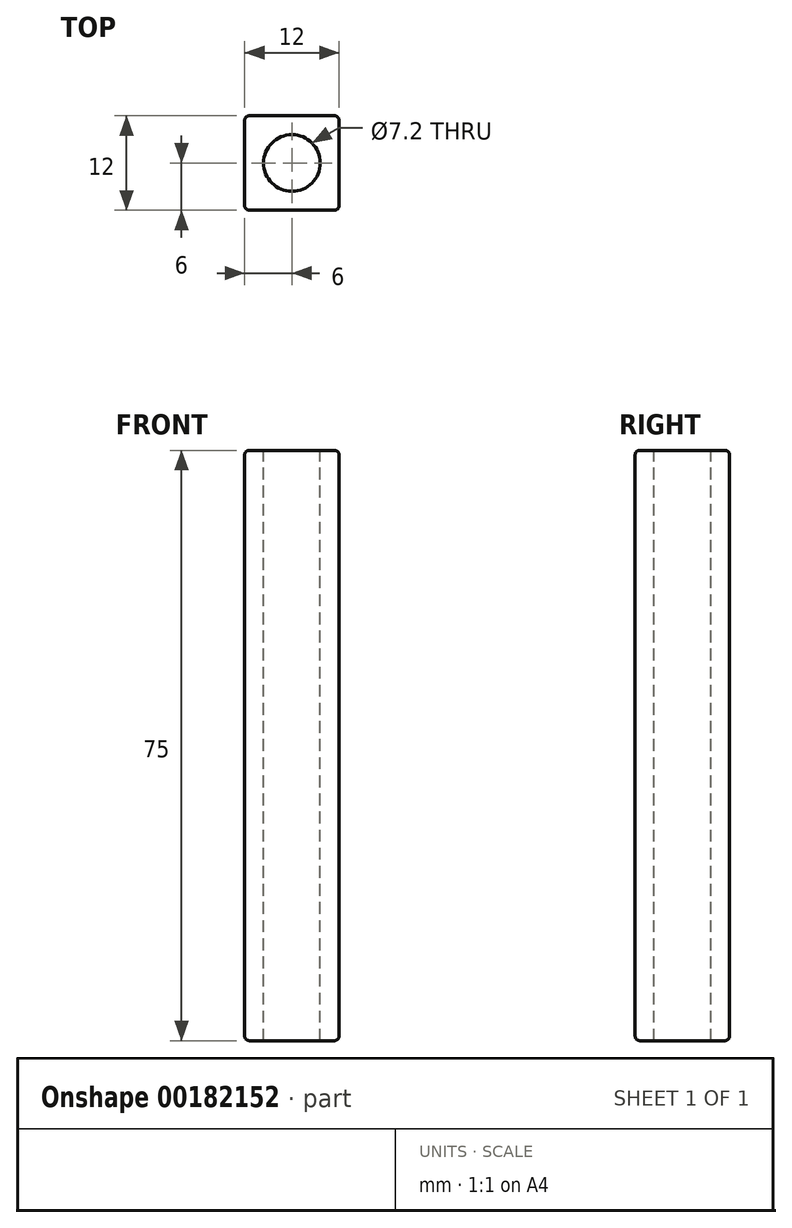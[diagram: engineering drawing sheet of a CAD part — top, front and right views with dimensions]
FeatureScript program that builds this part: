
annotation { "Feature Type Name" : "Feature", "Feature Type Description" : "" }
export const myFeature = defineFeature(function(context is Context, id is Id, definition is map)
    precondition{}
    {
        {
            var Q0;
            Q0=qCreatedBy(makeId("Top.planeOp"),FACE);
            var sketch = newSketch(context, id + "F0", { "sketchPlane" : qUnion([Q0])});
            skLineSegment(sketch, "E0.bottom", {"start": v(6, -6) * mm, "end": v(-6, -6) * mm});
            skLineSegment(sketch, "E0.top", {"start": v(6, 6) * mm, "end": v(-6, 6) * mm});
            skLineSegment(sketch, "E0.left", {"start": v(6, -6) * mm, "end": v(6, 6) * mm});
            skLineSegment(sketch, "E0.right", {"start": v(-6, -6) * mm, "end": v(-6, 6) * mm});
            skPoint(sketch, "E0.middle", {"position": v(0, 0) * mm});
            skSolve(sketch);
        }
        {
            var Q0;
            Q0 = qSketchRegion(id + "F0", true);
            extrude(context, id + "F1", {"entities" : qUnion([Q0]), "depth" : 75 * mm});
        }
        {
            var Q0;
            Q0=makeQuery(id+"F1.opExtrude","CAP_FACE",FACE,{"disambiguationData":[OSD([sQuery(id+"F0.wireOp",EDGE,"E0.bottom"),sQuery(id+"F0.wireOp",EDGE,"E0.top"),sQuery(id+"F0.wireOp",EDGE,"E0.left"),sQuery(id+"F0.wireOp",EDGE,"E0.right")])],"isStart":false});
            var sketch = newSketch(context, id + "F2", { "sketchPlane" : qUnion([Q0])});
            skCircle(sketch, "E1", {"center": v(0, 0) * mm, "radius": 3.6 * mm});
            skSolve(sketch);
        }
        {
            var Q0;
            Q0 = qSketchRegion(id + "F2", true);
            extrude(context, id + "F3", {"entities" : qUnion([Q0]), "operationType" : NewBodyOperationType.REMOVE, "oppositeDirection" : true, "depth" : 80 * mm});
        }
        {
            var Q0;
            Q0=makeQuery(id+"F1.opExtrude","SWEPT_FACE",FACE,{"disambiguationData":[OSD([sQuery(id+"F0.wireOp",EDGE,"E0.bottom")])]});
            var Q1;
            Q1=makeQuery(id+"F1.opExtrude","SWEPT_FACE",FACE,{"disambiguationData":[OSD([sQuery(id+"F0.wireOp",EDGE,"E0.left")])]});
            var Q2;
            Q2=makeQuery(id+"F1.opExtrude","SWEPT_FACE",FACE,{"disambiguationData":[OSD([sQuery(id+"F0.wireOp",EDGE,"E0.top")])]});
            var Q3;
            Q3=makeQuery(id+"F1.opExtrude","SWEPT_FACE",FACE,{"disambiguationData":[OSD([sQuery(id+"F0.wireOp",EDGE,"E0.right")])]});
            fillet(context, id + "F4", {"entities" : qUnion([Q0, Q1, Q2, Q3]), "radius" : 0.6 * mm, "tangentPropagation" : true, "allowEdgeOverflow" : false});
        }
    });
